# Revit family: STL23425_27_30
name_source: partatom
category: Luminárias
units: mm (PartAtom-declared; Revit-internal decimal feet)

## family parameters
Com base no plano de trabalho = Não
Compartilhado = Não
Corte com vazios quando carregada = Não
Cota do conector redondo = Utilizar diâmetro
Fonte luminosa = Sim
Manter orientação da anotação = Não
Ponto de cálculo do ambiente = Não
Sempre na vertical = Sim
Tipo de parte = Normal

## types (2) — shared parameters
Altura = 0.07 m
Dimerização = 20-100%
Diâmetro = 0.07 m
Fabricante = Stella
Filtro de cor = 16777215
Grau de proteção (IP) = IP20
IRC (Índice de reprodução de cores) = >95 (R9>80)
Modelo = Lâmpada LED AR70 PRO 14°
Potência = 5 W
Tensão Elétrica = 100V-240V
Troca de temperatura da cor de lâmpada com esmaecimento = <Nenhum>
URL = https://stella.com.br
Ângulo de Abertura = 14°
Ângulo de inclinação = 90.00°
zero-valued in all types: Elevação padrão

## per-type parameters (varying)
| type | Arquivo de rede fotométrica | Fluxo Luminoso | Referência | Temperatura da cor (K) |
| STL23425/27 - BIVOLT - 2700K - 280lm - 14° | STELLA - STL23425-27 - AR70 PRO DIM 14°.ies | 280 lm | STL23425/27 | 2700 K |
| STL23425/30 - BIVOLT - 3000K - 300lm - 14° | STELLA - STL23425-30 - AR70 PRO DIM 14°.ies | 300 lm | STL23425/30 | 3000 K |
